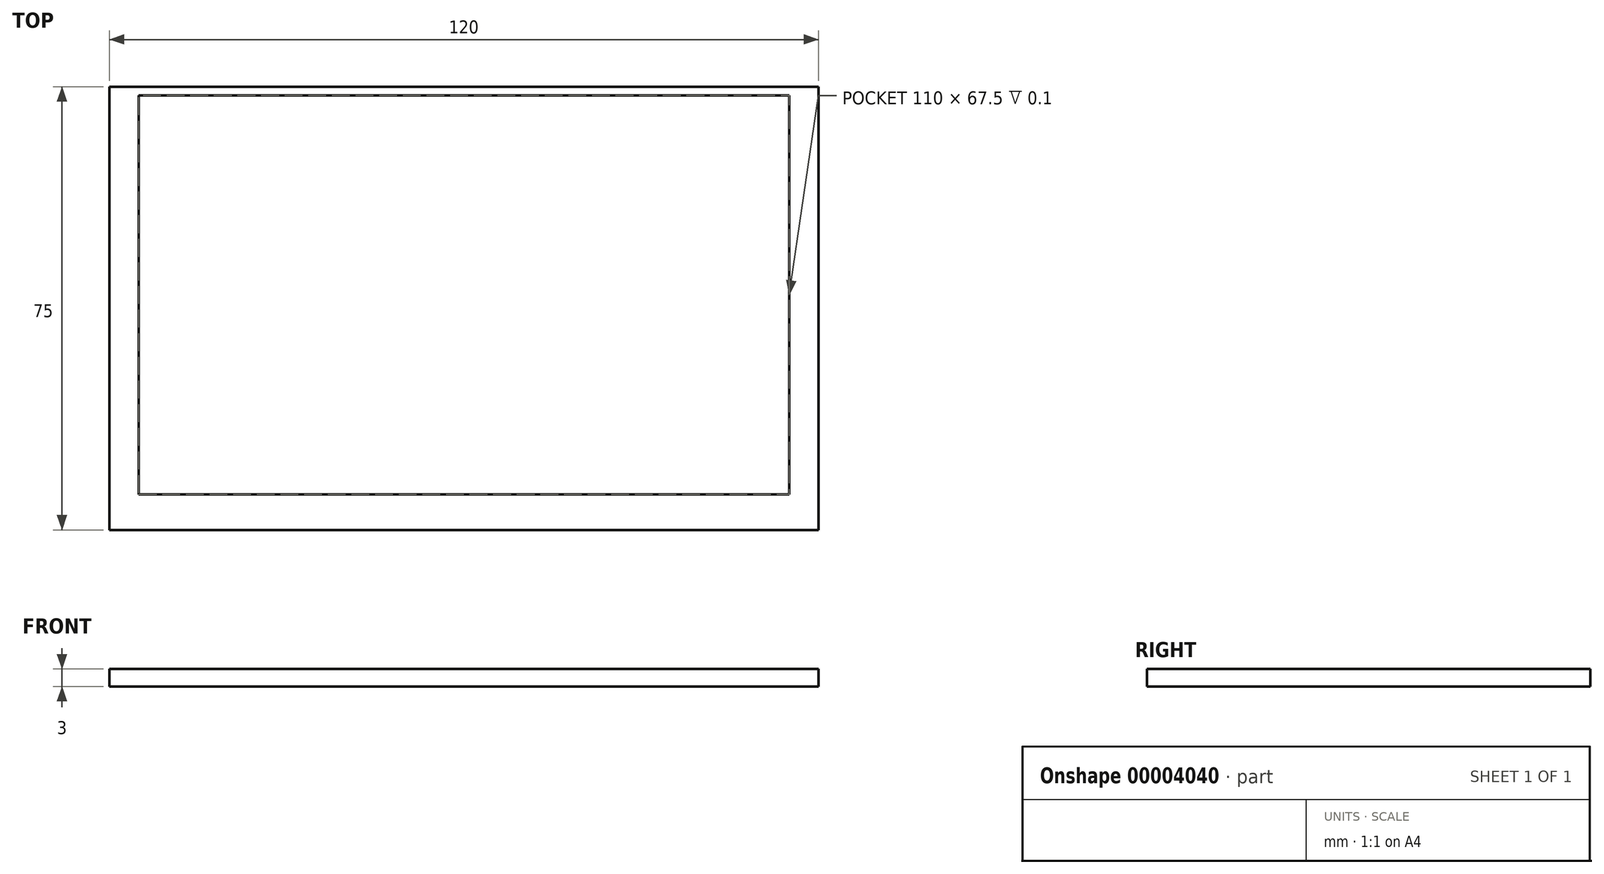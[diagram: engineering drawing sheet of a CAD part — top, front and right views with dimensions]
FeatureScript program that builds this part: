
annotation { "Feature Type Name" : "Feature", "Feature Type Description" : "" }
export const myFeature = defineFeature(function(context is Context, id is Id, definition is map)
    precondition{}
    {
        {
            var Q0;
            Q0=qCreatedBy(makeId("Top.planeOp"),FACE);
            var sketch = newSketch(context, id + "F0", { "sketchPlane" : qUnion([Q0])});
            skLineSegment(sketch, "E0.bottom", {"start": v(0, 75) * mm, "end": v(120, 75) * mm});
            skLineSegment(sketch, "E0.top", {"start": v(0, 0) * mm, "end": v(120, 0) * mm});
            skLineSegment(sketch, "E0.left", {"start": v(0, 75) * mm, "end": v(0, 0) * mm});
            skLineSegment(sketch, "E0.right", {"start": v(120, 75) * mm, "end": v(120, 0) * mm});
            skSolve(sketch);
        }
        {
            var Q0;
            Q0=makeQuery(id+"F0.imprint","IMPRINT",FACE,{"disambiguationData":[TD([[makeQuery(id+"F0.imprint","IMPRINT",EDGE,{"derivedFrom":sQuery(id+"F0.wireOp",EDGE,"E0.bottom")}),-1.0]])]});
            extrude(context, id + "F1", {"entities" : qUnion([Q0]), "depth" : 3 * mm});
        }
        {
            var Q0;
            Q0=makeQuery(id+"F1.opExtrude","CAP_FACE",FACE,{"disambiguationData":[OSD([sQuery(id+"F0.wireOp",EDGE,"E0.bottom"),sQuery(id+"F0.wireOp",EDGE,"E0.top"),sQuery(id+"F0.wireOp",EDGE,"E0.left"),sQuery(id+"F0.wireOp",EDGE,"E0.right")])],"isStart":false});
            var sketch = newSketch(context, id + "F2", { "sketchPlane" : qUnion([Q0])});
            skLineSegment(sketch, "E1.bottom", {"start": v(5, 73.5) * mm, "end": v(115, 73.5) * mm});
            skLineSegment(sketch, "E1.top", {"start": v(5, 6) * mm, "end": v(115, 6) * mm});
            skLineSegment(sketch, "E1.left", {"start": v(5, 73.5) * mm, "end": v(5, 6) * mm});
            skLineSegment(sketch, "E1.right", {"start": v(115, 73.5) * mm, "end": v(115, 6) * mm});
            skLineSegment(sketch, "E2.0", {"start": v(0, 75) * mm, "end": v(120, 75) * mm});
            skLineSegment(sketch, "E3.0", {"start": v(120, 75) * mm, "end": v(120, 0) * mm});
            skLineSegment(sketch, "E4.0", {"start": v(0, 0) * mm, "end": v(120, 0) * mm});
            skLineSegment(sketch, "E5.0", {"start": v(0, 75) * mm, "end": v(0, 0) * mm});
            skSolve(sketch);
        }
        {
            var Q0;
            Q0=makeQuery(id+"F2.imprint","IMPRINT",FACE,{"disambiguationData":[TD([[makeQuery(id+"F2.imprint","IMPRINT",EDGE,{"derivedFrom":sQuery(id+"F2.wireOp",EDGE,"E1.bottom")}),-1.0]])]});
            extrude(context, id + "F3", {"entities" : qUnion([Q0]), "operationType" : NewBodyOperationType.REMOVE, "oppositeDirection" : true, "depth" : 0.1 * mm});
        }
    });
